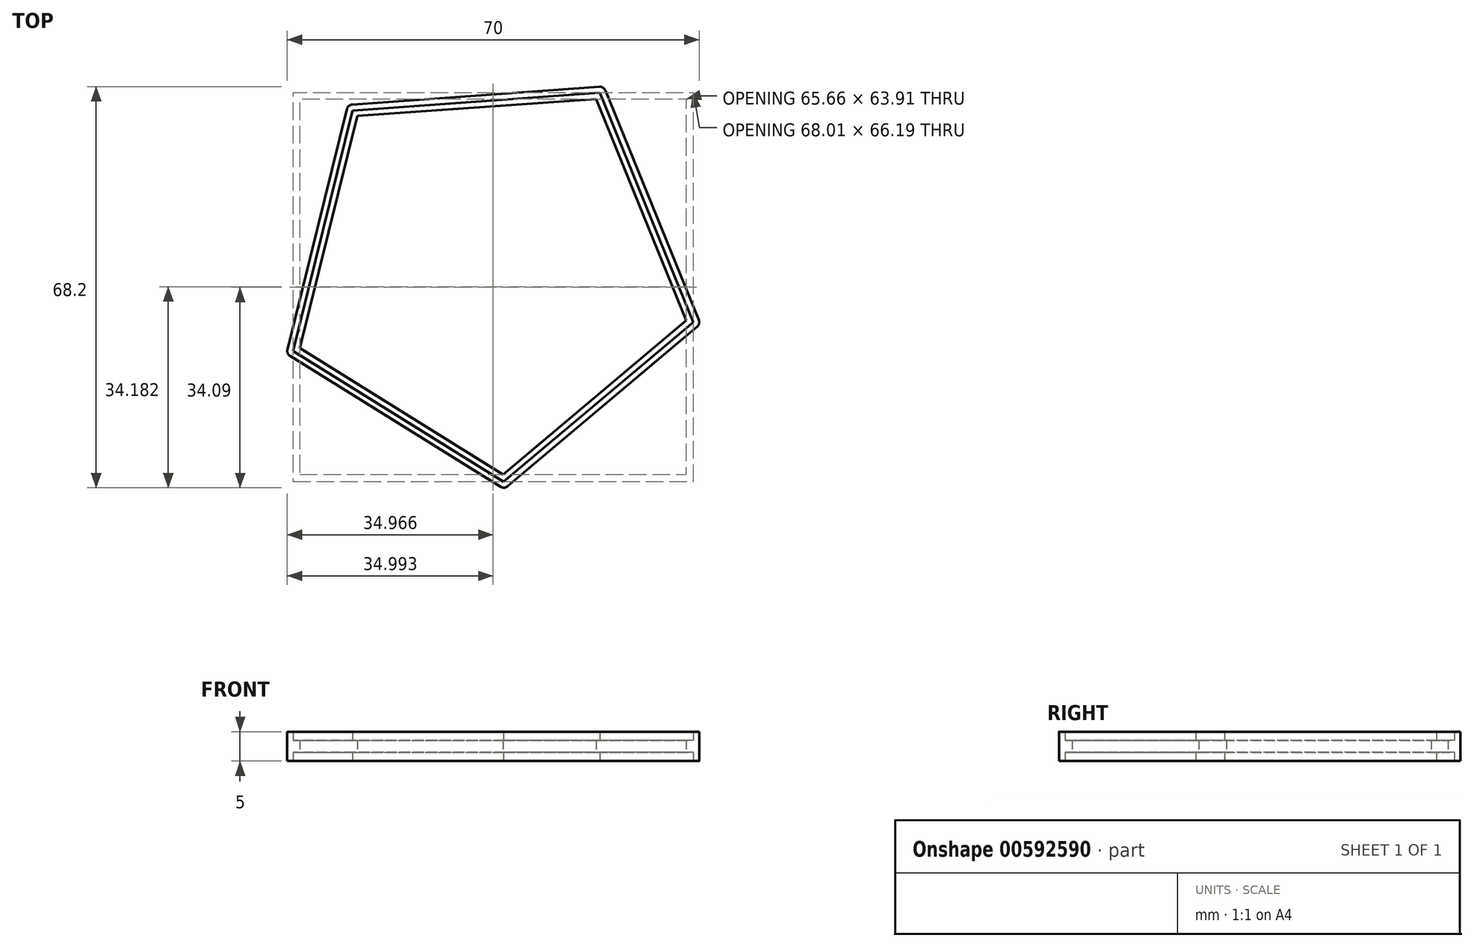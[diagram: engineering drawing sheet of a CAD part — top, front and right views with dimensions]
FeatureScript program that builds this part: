
annotation { "Feature Type Name" : "Feature", "Feature Type Description" : "" }
export const myFeature = defineFeature(function(context is Context, id is Id, definition is map)
    precondition{}
    {
        {
            var Q0;
            Q0=qCreatedBy(makeId("Top.planeOp"),FACE);
            var sketch = newSketch(context, id + "F0", { "sketchPlane" : qUnion([Q0])});
            skLineSegment(sketch, "E0.0", {"start": v(-23.9, 28.35) * mm, "end": v(19.57, 31.5) * mm});
            skLineSegment(sketch, "E0.1", {"start": v(19.57, 31.5) * mm, "end": v(36, -8.88) * mm});
            skLineSegment(sketch, "E0.2", {"start": v(36, -8.88) * mm, "end": v(2.68, -36.99) * mm});
            skLineSegment(sketch, "E0.3", {"start": v(2.68, -36.99) * mm, "end": v(-34.35, -13.98) * mm});
            skLineSegment(sketch, "E0.4", {"start": v(-34.35, -13.98) * mm, "end": v(-23.9, 28.35) * mm});
            skPoint(sketch, "E0.0.midPoint", {"position": v(-2.17, 29.92) * mm});
            skLineSegment(sketch, "E1.0", {"start": v(-23.1, 27.42) * mm, "end": v(18.94, 30.43) * mm});
            skLineSegment(sketch, "E1.1", {"start": v(18.94, 30.43) * mm, "end": v(34.8, -8.6) * mm});
            skLineSegment(sketch, "E1.2", {"start": v(34.8, -8.6) * mm, "end": v(2.57, -35.75) * mm});
            skLineSegment(sketch, "E1.3", {"start": v(2.57, -35.75) * mm, "end": v(-33.21, -13.5) * mm});
            skLineSegment(sketch, "E1.4", {"start": v(-33.21, -13.5) * mm, "end": v(-23.1, 27.42) * mm});
            skPoint(sketch, "E1.0.midPoint", {"position": v(-2.08, 28.93) * mm});
            skLineSegment(sketch, "E2.0", {"start": v(-22.3, 26.47) * mm, "end": v(18.29, 29.39) * mm});
            skLineSegment(sketch, "E2.1", {"start": v(18.29, 29.39) * mm, "end": v(33.6, -8.31) * mm});
            skLineSegment(sketch, "E2.2", {"start": v(33.6, -8.31) * mm, "end": v(2.48, -34.52) * mm});
            skLineSegment(sketch, "E2.3", {"start": v(2.48, -34.52) * mm, "end": v(-32.07, -13.02) * mm});
            skLineSegment(sketch, "E2.4", {"start": v(-32.07, -13.02) * mm, "end": v(-22.3, 26.47) * mm});
            skPoint(sketch, "E2.0.midPoint", {"position": v(-2, 27.93) * mm});
            skLineSegment(sketch, "E3.0", {"start": v(-22.84, 27.22) * mm, "end": v(18.83, 30.14) * mm});
            skLineSegment(sketch, "E3.1", {"start": v(18.83, 30.14) * mm, "end": v(34.48, -8.6) * mm});
            skLineSegment(sketch, "E3.2", {"start": v(34.48, -8.6) * mm, "end": v(2.48, -35.45) * mm});
            skLineSegment(sketch, "E3.3", {"start": v(2.48, -35.45) * mm, "end": v(-32.95, -13.31) * mm});
            skLineSegment(sketch, "E3.4", {"start": v(-32.95, -13.31) * mm, "end": v(-22.84, 27.22) * mm});
            skPoint(sketch, "E3.0.midPoint", {"position": v(-2, 28.68) * mm});
            skSolve(sketch);
        }
        {
            var Q0;
            Q0=makeQuery(id+"F0.imprint","IMPRINT",FACE,{"disambiguationData":[TD([[makeQuery(id+"F0.imprint","IMPRINT",EDGE,{"derivedFrom":sQuery(id+"F0.wireOp",EDGE,"E0.0")}),-1.0]])]});
            var Q1;
            Q1=makeQuery(id+"F0.imprint","IMPRINT",FACE,{"disambiguationData":[TD([[makeQuery(id+"F0.imprint","IMPRINT",EDGE,{"derivedFrom":sQuery(id+"F0.wireOp",EDGE,"E2.0")}),1.0]])]});
            var Q2;
            Q2=makeQuery(id+"F0.imprint","IMPRINT",FACE,{"disambiguationData":[TD([[makeQuery(id+"F0.imprint","IMPRINT",EDGE,{"derivedFrom":sQuery(id+"F0.wireOp",EDGE,"E1.0")}),-1.0]])]});
            extrude(context, id + "F1", {"entities" : qUnion([Q0, Q1, Q2]), "endBound" : BoundingType.SYMMETRIC, "depth" : 2 * mm, "offsetDistance" : 25 * mm});
        }
        {
            var Q0;
            Q0=makeQuery(id+"F0.imprint","IMPRINT",FACE,{"disambiguationData":[TD([[makeQuery(id+"F0.imprint","IMPRINT",EDGE,{"derivedFrom":sQuery(id+"F0.wireOp",EDGE,"E0.0")}),-1.0]])]});
            extrude(context, id + "F2", {"entities" : qUnion([Q0]), "operationType" : NewBodyOperationType.ADD, "endBound" : BoundingType.SYMMETRIC, "depth" : 5 * mm, "offsetDistance" : 25 * mm});
        }
        {
            var Q0;
            {var subQ0=sQuery(id+"F0.wireOp",EDGE,"E0.2");var subQ1=sQuery(id+"F0.wireOp",EDGE,"E0.1");Q0=makeQuery(id+"F2.boolean.opBoolean","MERGE",EDGE,{"derivedFrom":[makeQuery(id+"F1.opExtrude","SWEPT_EDGE",EDGE,{"disambiguationData":[OSD([subQ1,subQ0])]}),makeQuery(id+"F2.opExtrude","SWEPT_EDGE",EDGE,{"disambiguationData":[OSD([subQ1,subQ0])]})]});}
            var Q1;
            {var subQ0=sQuery(id+"F0.wireOp",EDGE,"E0.3");var subQ1=sQuery(id+"F0.wireOp",EDGE,"E0.2");Q1=makeQuery(id+"F2.boolean.opBoolean","MERGE",EDGE,{"derivedFrom":[makeQuery(id+"F1.opExtrude","SWEPT_EDGE",EDGE,{"disambiguationData":[OSD([subQ1,subQ0])]}),makeQuery(id+"F2.opExtrude","SWEPT_EDGE",EDGE,{"disambiguationData":[OSD([subQ1,subQ0])]})]});}
            var Q2;
            {var subQ0=sQuery(id+"F0.wireOp",EDGE,"E0.4");var subQ1=sQuery(id+"F0.wireOp",EDGE,"E0.3");Q2=makeQuery(id+"F2.boolean.opBoolean","MERGE",EDGE,{"derivedFrom":[makeQuery(id+"F1.opExtrude","SWEPT_EDGE",EDGE,{"disambiguationData":[OSD([subQ1,subQ0])]}),makeQuery(id+"F2.opExtrude","SWEPT_EDGE",EDGE,{"disambiguationData":[OSD([subQ1,subQ0])]})]});}
            var Q3;
            {var subQ0=sQuery(id+"F0.wireOp",EDGE,"E0.4");var subQ1=sQuery(id+"F0.wireOp",EDGE,"E0.0");Q3=makeQuery(id+"F2.boolean.opBoolean","MERGE",EDGE,{"derivedFrom":[makeQuery(id+"F1.opExtrude","SWEPT_EDGE",EDGE,{"disambiguationData":[OSD([subQ1,subQ0])]}),makeQuery(id+"F2.opExtrude","SWEPT_EDGE",EDGE,{"disambiguationData":[OSD([subQ1,subQ0])]})]});}
            var Q4;
            {var subQ0=sQuery(id+"F0.wireOp",EDGE,"E0.1");var subQ1=sQuery(id+"F0.wireOp",EDGE,"E0.0");Q4=makeQuery(id+"F2.boolean.opBoolean","MERGE",EDGE,{"derivedFrom":[makeQuery(id+"F1.opExtrude","SWEPT_EDGE",EDGE,{"disambiguationData":[OSD([subQ1,subQ0])]}),makeQuery(id+"F2.opExtrude","SWEPT_EDGE",EDGE,{"disambiguationData":[OSD([subQ1,subQ0])]})]});}
            fillet(context, id + "F3", {"entities" : qUnion([Q0, Q1, Q2, Q3, Q4]), "radius" : 1 * mm, "tangentPropagation" : true, "allowEdgeOverflow" : false});
        }
    });
